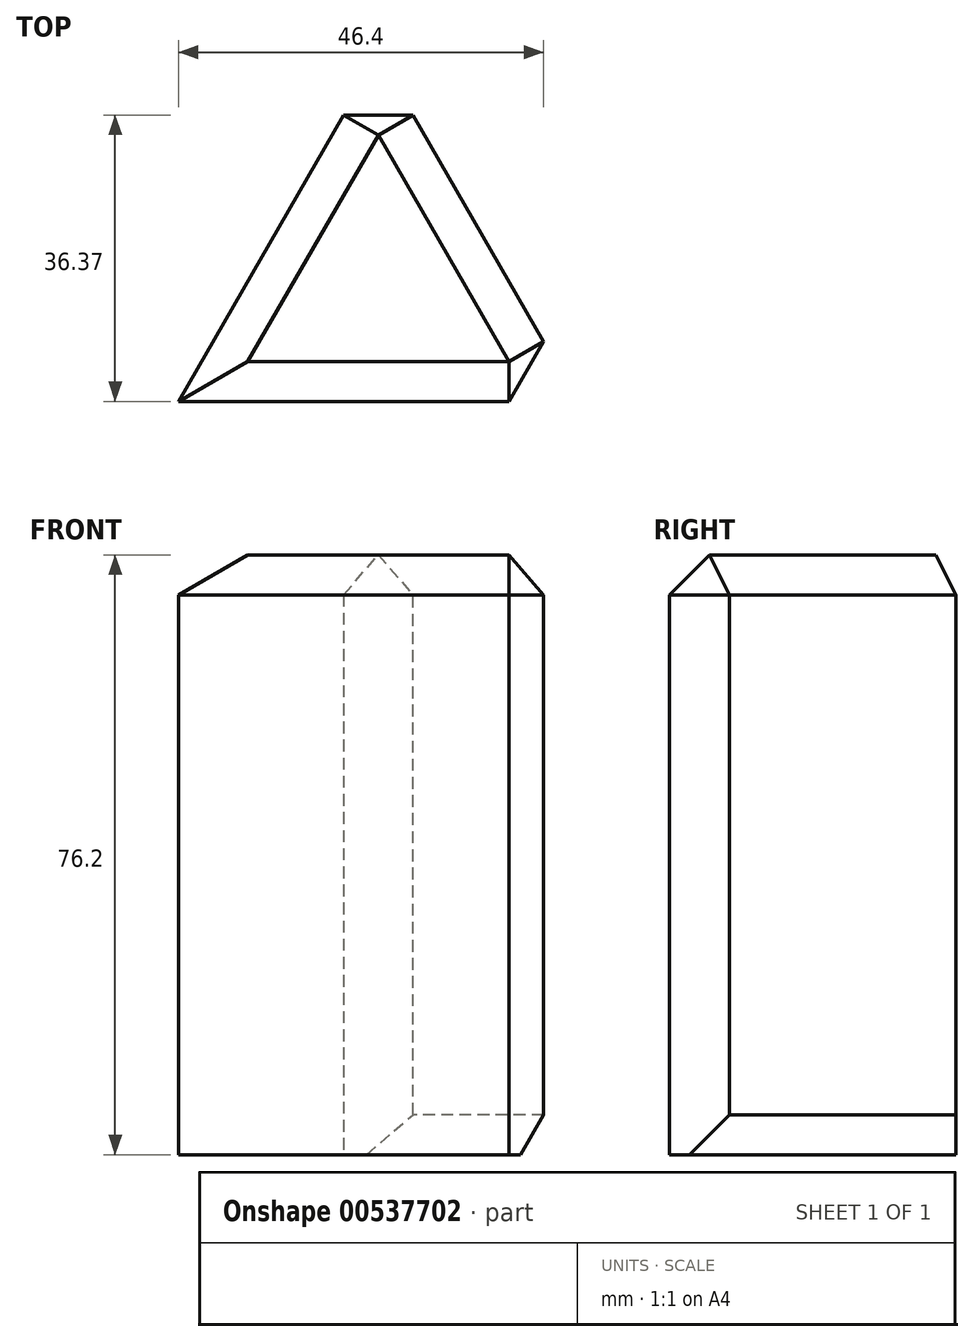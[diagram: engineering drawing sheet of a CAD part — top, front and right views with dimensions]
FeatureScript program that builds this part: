
annotation { "Feature Type Name" : "Feature", "Feature Type Description" : "" }
export const myFeature = defineFeature(function(context is Context, id is Id, definition is map)
    precondition{}
    {
        {
            var Q0;
            Q0=qCreatedBy(makeId("Top.planeOp"),FACE);
            var sketch = newSketch(context, id + "F0", { "sketchPlane" : qUnion([Q0])});
            skLineSegment(sketch, "E0", {"start": v(0, 44) * mm, "end": v(-25.4, 0) * mm});
            skLineSegment(sketch, "E1", {"start": v(-25.4, 0) * mm, "end": v(25.4, 0) * mm});
            skLineSegment(sketch, "E2", {"start": v(25.4, 0) * mm, "end": v(0, 44) * mm});
            skSolve(sketch);
        }
        {
            var Q0;
            Q0 = qSketchRegion(id + "F0", true);
            extrude(context, id + "F1", {"entities" : qUnion([Q0]), "depth" : 76.2 * mm, "offsetDistance" : 25.4 * mm});
        }
        {
            var Q0;
            Q0=makeQuery(id+"F1.opExtrude","CAP_EDGE",EDGE,{"disambiguationData":[OSD([sQuery(id+"F0.wireOp",EDGE,"E2")])],"isStart":false});
            var Q1;
            Q1=makeQuery(id+"F1.opExtrude","CAP_FACE",FACE,{"disambiguationData":[OSD([sQuery(id+"F0.wireOp",EDGE,"E0"),sQuery(id+"F0.wireOp",EDGE,"E1"),sQuery(id+"F0.wireOp",EDGE,"E2")])],"isStart":false});
            var Q2;
            Q2=makeQuery(id+"F1.opExtrude","SWEPT_FACE",FACE,{"disambiguationData":[OSD([sQuery(id+"F0.wireOp",EDGE,"E2")])]});
            chamfer(context, id + "F2", {"entities" : qUnion([Q0, Q1, Q2]), "width" : 5.08 * mm, "tangentPropagation" : true});
        }
    });
